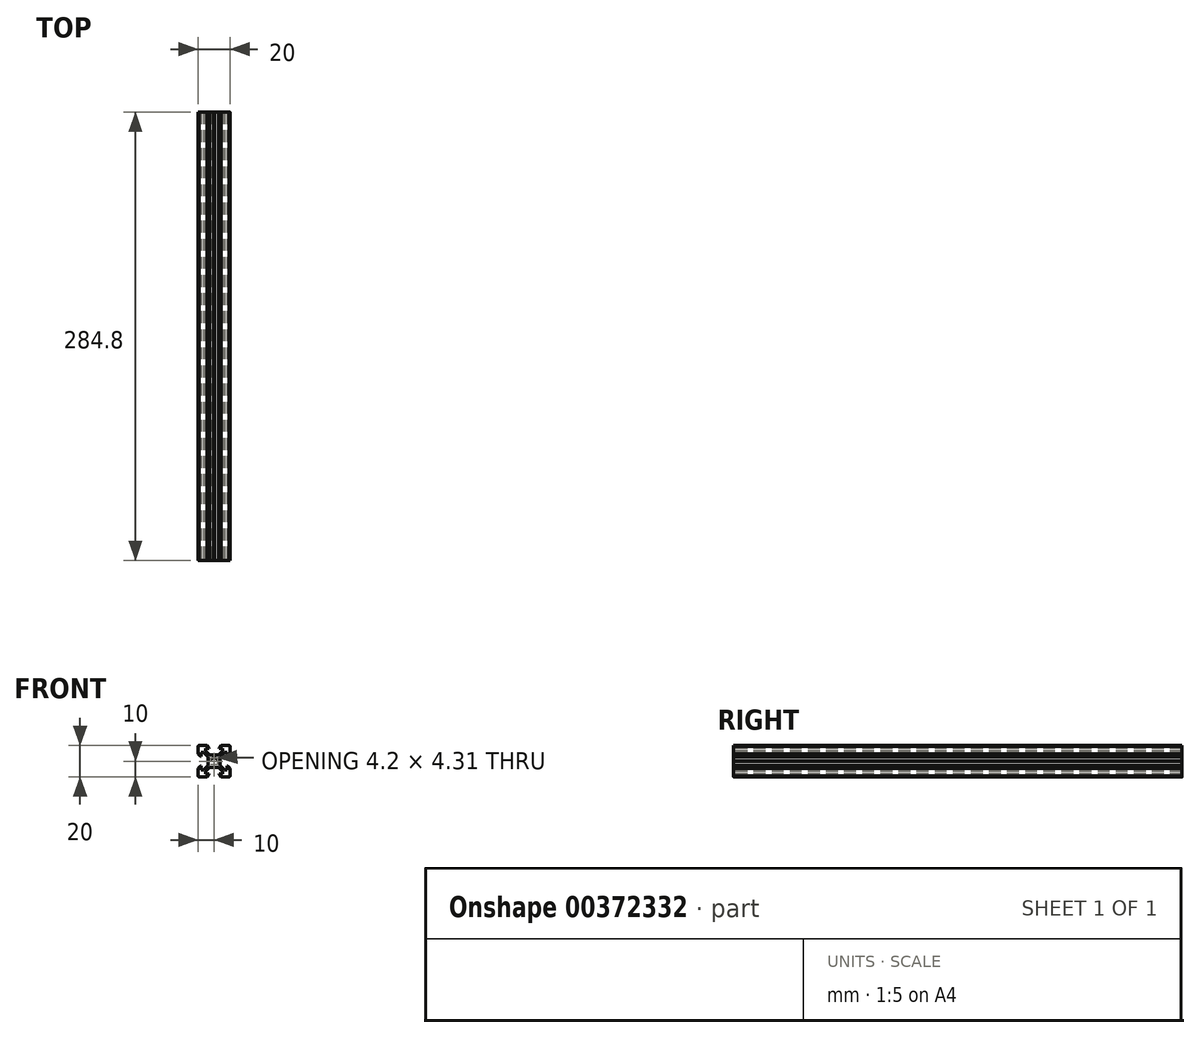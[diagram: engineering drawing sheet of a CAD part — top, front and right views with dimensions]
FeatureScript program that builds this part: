
annotation { "Feature Type Name" : "Feature", "Feature Type Description" : "" }
export const myFeature = defineFeature(function(context is Context, id is Id, definition is map)
    precondition{}
    {
        {
            var Q0;
            Q0=qCreatedBy(makeId("Front.planeOp"),FACE);
            var sketch = newSketch(context, id + "F0", { "sketchPlane" : qUnion([Q0])});
            skFitSpline(sketch, "E0.0", {"points": [v(-8.2, 3.13) * mm, v(-8.2, 3.92) * mm, v(-8.2, 4.7) * mm, v(-8.2, 5.5) * mm]});
            skFitSpline(sketch, "E0.1", {"points": [v(-8.2, 5.5) * mm, v(-7.65, 5.5) * mm, v(-7.1, 5.5) * mm, v(-6.56, 5.5) * mm]});
            skFitSpline(sketch, "E0.2", {"points": [v(-6.56, 5.5) * mm, v(-5.67, 4.61) * mm, v(-4.79, 3.73) * mm, v(-3.9, 2.84) * mm]});
            skFitSpline(sketch, "E0.3", {"points": [v(-2.84, 3.9) * mm, v(-3.73, 4.79) * mm, v(-4.61, 5.67) * mm, v(-5.5, 6.56) * mm]});
            skFitSpline(sketch, "E0.4", {"points": [v(-5.5, 6.56) * mm, v(-5.5, 7.1) * mm, v(-5.5, 7.65) * mm, v(-5.5, 8.2) * mm]});
            skFitSpline(sketch, "E0.5", {"points": [v(-5.5, 8.2) * mm, v(-4.7, 8.2) * mm, v(-3.92, 8.2) * mm, v(-3.12, 8.2) * mm]});
            skFitSpline(sketch, "E0.6", {"points": [v(-3.12, 8.2) * mm, v(-3.12, 8.32) * mm, v(-3.12, 8.43) * mm, v(-3.12, 8.55) * mm]});
            skFitSpline(sketch, "E0.7", {"points": [v(-10, 4.58) * mm, v(-9.51, 4.1) * mm, v(-9.03, 3.61) * mm, v(-8.54, 3.13) * mm]});
            skFitSpline(sketch, "E0.8", {"points": [v(-8.54, 3.13) * mm, v(-8.43, 3.13) * mm, v(-8.31, 3.13) * mm, v(-8.2, 3.13) * mm]});
            skFitSpline(sketch, "E0.9", {"points": [v(-10, 9.5) * mm, v(-10, 7.86) * mm, v(-10, 6.22) * mm, v(-10, 4.58) * mm]});
            skFitSpline(sketch, "E0.10", {"points": [v(-9.5, 10) * mm, v(-9.57, 10) * mm, v(-9.63, 9.99) * mm, v(-9.7, 9.96) * mm, v(-9.75, 9.94) * mm, v(-9.8, 9.9) * mm, v(-9.85, 9.85) * mm, v(-9.9, 9.8) * mm, v(-9.94, 9.75) * mm, v(-9.96, 9.7) * mm, v(-9.99, 9.63) * mm, v(-10, 9.57) * mm, v(-10, 9.5) * mm]});
            skFitSpline(sketch, "E0.11", {"points": [v(-4.58, 10) * mm, v(-6.22, 10) * mm, v(-7.86, 10) * mm, v(-9.5, 10) * mm]});
            skFitSpline(sketch, "E0.12", {"points": [v(-3.9, 2.84) * mm, v(-3.9, 1.96) * mm, v(-3.9, 1.09) * mm, v(-3.9, 0.21) * mm]});
            skFitSpline(sketch, "E0.13", {"points": [v(-3.9, 0.21) * mm, v(-3.83, 0.14) * mm, v(-3.76, 0.07) * mm, v(-3.69, 0) * mm]});
            skFitSpline(sketch, "E0.14", {"points": [v(-0.2, 3.9) * mm, v(-1.09, 3.9) * mm, v(-1.96, 3.9) * mm, v(-2.84, 3.9) * mm]});
            skFitSpline(sketch, "E0.15", {"points": [v(0, 3.7) * mm, v(-0.07, 3.76) * mm, v(-0.14, 3.83) * mm, v(-0.2, 3.9) * mm]});
            skFitSpline(sketch, "E0.16", {"points": [v(2.1, 0) * mm, v(2.1, 0.27) * mm, v(2, 0.82) * mm, v(1.52, 1.52) * mm, v(0.82, 2) * mm, v(0, 2.15) * mm, v(-0.82, 2) * mm, v(-1.52, 1.52) * mm, v(-2, 0.82) * mm, v(-2.1, 0.27) * mm, v(-2.1, 0) * mm]});
            skFitSpline(sketch, "E1.0", {"points": [v(-8.2, 3.13) * mm, v(-8.2, 3.92) * mm, v(-8.2, 4.7) * mm, v(-8.2, 5.5) * mm]});
            skFitSpline(sketch, "E1.1", {"points": [v(-8.2, 5.5) * mm, v(-7.65, 5.5) * mm, v(-7.1, 5.5) * mm, v(-6.56, 5.5) * mm]});
            skFitSpline(sketch, "E1.2", {"points": [v(-6.56, 5.5) * mm, v(-5.67, 4.61) * mm, v(-4.79, 3.73) * mm, v(-3.9, 2.84) * mm]});
            skFitSpline(sketch, "E1.3", {"points": [v(-2.84, 3.9) * mm, v(-3.73, 4.79) * mm, v(-4.61, 5.67) * mm, v(-5.5, 6.56) * mm]});
            skFitSpline(sketch, "E1.4", {"points": [v(-5.5, 6.56) * mm, v(-5.5, 7.1) * mm, v(-5.5, 7.65) * mm, v(-5.5, 8.2) * mm]});
            skFitSpline(sketch, "E1.5", {"points": [v(-5.5, 8.2) * mm, v(-4.7, 8.2) * mm, v(-3.92, 8.2) * mm, v(-3.12, 8.2) * mm]});
            skFitSpline(sketch, "E1.6", {"points": [v(-3.12, 8.2) * mm, v(-3.12, 8.32) * mm, v(-3.12, 8.43) * mm, v(-3.12, 8.55) * mm]});
            skFitSpline(sketch, "E1.7", {"points": [v(-10, 4.58) * mm, v(-9.51, 4.1) * mm, v(-9.03, 3.61) * mm, v(-8.54, 3.13) * mm]});
            skFitSpline(sketch, "E1.8", {"points": [v(-8.54, 3.13) * mm, v(-8.43, 3.13) * mm, v(-8.31, 3.13) * mm, v(-8.2, 3.13) * mm]});
            skFitSpline(sketch, "E1.9", {"points": [v(-10, 9.5) * mm, v(-10, 7.86) * mm, v(-10, 6.22) * mm, v(-10, 4.58) * mm]});
            skFitSpline(sketch, "E1.10", {"points": [v(-9.5, 10) * mm, v(-9.57, 10) * mm, v(-9.63, 9.99) * mm, v(-9.7, 9.96) * mm, v(-9.75, 9.94) * mm, v(-9.8, 9.9) * mm, v(-9.85, 9.85) * mm, v(-9.9, 9.8) * mm, v(-9.94, 9.75) * mm, v(-9.96, 9.7) * mm, v(-9.99, 9.63) * mm, v(-10, 9.57) * mm, v(-10, 9.5) * mm]});
            skFitSpline(sketch, "E1.11", {"points": [v(-4.58, 10) * mm, v(-6.22, 10) * mm, v(-7.86, 10) * mm, v(-9.5, 10) * mm]});
            skFitSpline(sketch, "E1.12", {"points": [v(-3.9, 2.84) * mm, v(-3.9, 1.96) * mm, v(-3.9, 1.09) * mm, v(-3.9, 0.21) * mm]});
            skFitSpline(sketch, "E1.13", {"points": [v(-3.9, 0.21) * mm, v(-3.83, 0.14) * mm, v(-3.76, 0.07) * mm, v(-3.69, 0) * mm]});
            skFitSpline(sketch, "E1.14", {"points": [v(-0.2, 3.9) * mm, v(-1.09, 3.9) * mm, v(-1.96, 3.9) * mm, v(-2.84, 3.9) * mm]});
            skFitSpline(sketch, "E1.15", {"points": [v(0, 3.7) * mm, v(-0.07, 3.76) * mm, v(-0.14, 3.83) * mm, v(-0.2, 3.9) * mm]});
            skFitSpline(sketch, "E1.16", {"points": [v(2.1, 0) * mm, v(2.1, 0.27) * mm, v(2, 0.82) * mm, v(1.52, 1.52) * mm, v(0.82, 2) * mm, v(0, 2.15) * mm, v(-0.82, 2) * mm, v(-1.52, 1.52) * mm, v(-2, 0.82) * mm, v(-2.1, 0.27) * mm, v(-2.1, 0) * mm]});
            skFitSpline(sketch, "E2.0", {"points": [v(2.84, 3.9) * mm, v(1.96, 3.9) * mm, v(1.09, 3.9) * mm, v(0.21, 3.9) * mm]});
            skFitSpline(sketch, "E2.1", {"points": [v(0.21, 3.9) * mm, v(0.14, 3.83) * mm, v(0.07, 3.76) * mm, v(0, 3.7) * mm]});
            skFitSpline(sketch, "E2.2", {"points": [v(3.9, 0.2) * mm, v(3.9, 1.09) * mm, v(3.9, 1.96) * mm, v(3.9, 2.84) * mm]});
            skFitSpline(sketch, "E2.3", {"points": [v(3.69, 0) * mm, v(3.76, 0.07) * mm, v(3.83, 0.14) * mm, v(3.9, 0.2) * mm]});
            skFitSpline(sketch, "E2.4", {"points": [v(3.9, 2.84) * mm, v(4.79, 3.73) * mm, v(5.67, 4.61) * mm, v(6.56, 5.5) * mm]});
            skFitSpline(sketch, "E2.5", {"points": [v(5.5, 6.56) * mm, v(4.61, 5.67) * mm, v(3.73, 4.79) * mm, v(2.84, 3.9) * mm]});
            skFitSpline(sketch, "E2.6", {"points": [v(6.56, 5.5) * mm, v(7.1, 5.5) * mm, v(7.65, 5.5) * mm, v(8.2, 5.5) * mm]});
            skFitSpline(sketch, "E2.7", {"points": [v(8.2, 5.5) * mm, v(8.2, 4.7) * mm, v(8.2, 3.92) * mm, v(8.2, 3.13) * mm]});
            skFitSpline(sketch, "E2.8", {"points": [v(8.2, 3.13) * mm, v(8.31, 3.13) * mm, v(8.43, 3.13) * mm, v(8.54, 3.13) * mm]});
            skFitSpline(sketch, "E2.9", {"points": [v(8.54, 3.13) * mm, v(9.03, 3.61) * mm, v(9.51, 4.1) * mm, v(10, 4.58) * mm]});
            skFitSpline(sketch, "E2.10", {"points": [v(10, 4.58) * mm, v(10, 6.22) * mm, v(10, 7.86) * mm, v(10, 9.5) * mm]});
            skFitSpline(sketch, "E2.11", {"points": [v(5.5, 8.2) * mm, v(5.5, 7.65) * mm, v(5.5, 7.1) * mm, v(5.5, 6.56) * mm]});
            skFitSpline(sketch, "E2.12", {"points": [v(3.13, 8.2) * mm, v(3.92, 8.2) * mm, v(4.7, 8.2) * mm, v(5.5, 8.2) * mm]});
            skFitSpline(sketch, "E2.13", {"points": [v(3.13, 8.55) * mm, v(3.13, 8.43) * mm, v(3.13, 8.32) * mm, v(3.13, 8.2) * mm]});
            skFitSpline(sketch, "E2.14", {"points": [v(9.5, 10) * mm, v(7.86, 10) * mm, v(6.22, 10) * mm, v(4.58, 10) * mm]});
            skFitSpline(sketch, "E2.15", {"points": [v(10, 9.5) * mm, v(10, 9.57) * mm, v(9.99, 9.63) * mm, v(9.96, 9.7) * mm, v(9.94, 9.75) * mm, v(9.9, 9.8) * mm, v(9.85, 9.85) * mm, v(9.8, 9.9) * mm, v(9.75, 9.94) * mm, v(9.7, 9.96) * mm, v(9.63, 9.99) * mm, v(9.57, 10) * mm, v(9.5, 10) * mm]});
            skFitSpline(sketch, "E2.16", {"points": [v(4.58, 10) * mm, v(4.1, 9.52) * mm, v(3.61, 9.03) * mm, v(3.13, 8.55) * mm]});
            skLineSegment(sketch, "E3", {"start": v(-4.58, 10) * mm, "end": v(-3.12, 8.55) * mm});
            skFitSpline(sketch, "E4.MirrorCS", {"points": [v(-3.9, -0.2) * mm, v(-3.83, -0.14) * mm, v(-3.76, -0.07) * mm, v(-3.69, 0) * mm]});
            skFitSpline(sketch, "E5.MirrorCS", {"points": [v(0, -3.7) * mm, v(-0.07, -3.76) * mm, v(-0.14, -3.83) * mm, v(-0.21, -3.9) * mm]});
            skFitSpline(sketch, "E6.MirrorCS", {"points": [v(-8.55, -3.12) * mm, v(-8.43, -3.12) * mm, v(-8.32, -3.12) * mm, v(-8.2, -3.12) * mm]});
            skFitSpline(sketch, "E7.MirrorCS", {"points": [v(0.2, -3.9) * mm, v(0.14, -3.83) * mm, v(0.07, -3.76) * mm, v(0, -3.7) * mm]});
            skFitSpline(sketch, "E8.MirrorCS", {"points": [v(-3.13, -8.2) * mm, v(-3.13, -8.31) * mm, v(-3.13, -8.43) * mm, v(-3.13, -8.54) * mm]});
            skFitSpline(sketch, "E9.MirrorCS", {"points": [v(-3.9, -0.2) * mm, v(-3.83, -0.14) * mm, v(-3.76, -0.07) * mm, v(-3.69, 0) * mm]});
            skFitSpline(sketch, "E10.MirrorCS", {"points": [v(-8.55, -3.12) * mm, v(-8.43, -3.12) * mm, v(-8.32, -3.12) * mm, v(-8.2, -3.12) * mm]});
            skFitSpline(sketch, "E11.MirrorCS", {"points": [v(0, -3.7) * mm, v(-0.07, -3.76) * mm, v(-0.14, -3.83) * mm, v(-0.21, -3.9) * mm]});
            skFitSpline(sketch, "E12.MirrorCS", {"points": [v(-3.13, -8.2) * mm, v(-3.13, -8.31) * mm, v(-3.13, -8.43) * mm, v(-3.13, -8.54) * mm]});
            skFitSpline(sketch, "E13.MirrorCS", {"points": [v(3.12, -8.55) * mm, v(3.12, -8.43) * mm, v(3.12, -8.32) * mm, v(3.12, -8.2) * mm]});
            skFitSpline(sketch, "E14.MirrorCS", {"points": [v(3.69, 0) * mm, v(3.76, -0.07) * mm, v(3.83, -0.14) * mm, v(3.9, -0.21) * mm]});
            skFitSpline(sketch, "E15.MirrorCS", {"points": [v(8.2, -3.13) * mm, v(8.31, -3.13) * mm, v(8.43, -3.13) * mm, v(8.54, -3.13) * mm]});
            skFitSpline(sketch, "E16.MirrorCS", {"points": [v(-8.2, -5.5) * mm, v(-7.65, -5.5) * mm, v(-7.1, -5.5) * mm, v(-6.56, -5.5) * mm]});
            skFitSpline(sketch, "E17.MirrorCS", {"points": [v(-2.84, -3.9) * mm, v(-3.73, -4.79) * mm, v(-4.61, -5.67) * mm, v(-5.5, -6.56) * mm]});
            skFitSpline(sketch, "E18.MirrorCS", {"points": [v(-5.5, -8.2) * mm, v(-4.7, -8.2) * mm, v(-3.92, -8.2) * mm, v(-3.13, -8.2) * mm]});
            skFitSpline(sketch, "E19.MirrorCS", {"points": [v(-5.5, -6.56) * mm, v(-5.5, -7.1) * mm, v(-5.5, -7.65) * mm, v(-5.5, -8.2) * mm]});
            skFitSpline(sketch, "E20.MirrorCS", {"points": [v(-0.21, -3.9) * mm, v(-1.09, -3.9) * mm, v(-1.96, -3.9) * mm, v(-2.84, -3.9) * mm]});
            skFitSpline(sketch, "E21.MirrorCS", {"points": [v(-8.2, -3.12) * mm, v(-8.2, -3.92) * mm, v(-8.2, -4.7) * mm, v(-8.2, -5.5) * mm]});
            skFitSpline(sketch, "E22.MirrorCS", {"points": [v(-10, -4.58) * mm, v(-9.52, -4.1) * mm, v(-9.03, -3.6) * mm, v(-8.55, -3.12) * mm]});
            skFitSpline(sketch, "E23.MirrorCS", {"points": [v(-10, -9.5) * mm, v(-10, -7.86) * mm, v(-10, -6.22) * mm, v(-10, -4.58) * mm]});
            skFitSpline(sketch, "E24.MirrorCS", {"points": [v(-9.5, -10) * mm, v(-9.57, -10) * mm, v(-9.63, -9.99) * mm, v(-9.7, -9.96) * mm, v(-9.75, -9.94) * mm, v(-9.8, -9.9) * mm, v(-9.85, -9.85) * mm, v(-9.9, -9.8) * mm, v(-9.94, -9.75) * mm, v(-9.96, -9.7) * mm, v(-9.99, -9.63) * mm, v(-10, -9.57) * mm, v(-10, -9.5) * mm]});
            skFitSpline(sketch, "E25.MirrorCS", {"points": [v(-4.58, -10) * mm, v(-6.22, -10) * mm, v(-7.86, -10) * mm, v(-9.5, -10) * mm]});
            skFitSpline(sketch, "E26.MirrorCS", {"points": [v(-3.9, -2.84) * mm, v(-3.9, -1.96) * mm, v(-3.9, -1.09) * mm, v(-3.9, -0.21) * mm]});
            skFitSpline(sketch, "E27.MirrorCS", {"points": [v(-6.56, -5.5) * mm, v(-5.67, -4.61) * mm, v(-4.79, -3.73) * mm, v(-3.9, -2.84) * mm]});
            skFitSpline(sketch, "E28.MirrorCS", {"points": [v(2.1, 0) * mm, v(2.1, -0.27) * mm, v(2, -0.82) * mm, v(1.52, -1.52) * mm, v(0.82, -2) * mm, v(0, -2.15) * mm, v(-0.82, -2) * mm, v(-1.52, -1.52) * mm, v(-2, -0.82) * mm, v(-2.1, -0.27) * mm, v(-2.1, 0) * mm]});
            skFitSpline(sketch, "E29.MirrorCS", {"points": [v(4.58, -10) * mm, v(4.1, -9.52) * mm, v(3.6, -9.03) * mm, v(3.12, -8.55) * mm]});
            skFitSpline(sketch, "E30.MirrorCS", {"points": [v(-6.56, -5.5) * mm, v(-5.67, -4.61) * mm, v(-4.79, -3.73) * mm, v(-3.9, -2.84) * mm]});
            skFitSpline(sketch, "E31.MirrorCS", {"points": [v(10, -4.58) * mm, v(10, -6.22) * mm, v(10, -7.86) * mm, v(10, -9.5) * mm]});
            skLineSegment(sketch, "E32.MirrorCS", {"start": v(-4.58, -10) * mm, "end": v(-3.13, -8.54) * mm});
            skFitSpline(sketch, "E33.MirrorCS", {"points": [v(-4.58, -10) * mm, v(-6.22, -10) * mm, v(-7.86, -10) * mm, v(-9.5, -10) * mm]});
            skFitSpline(sketch, "E34.MirrorCS", {"points": [v(6.56, -5.5) * mm, v(7.1, -5.5) * mm, v(7.65, -5.5) * mm, v(8.2, -5.5) * mm]});
            skFitSpline(sketch, "E35.MirrorCS", {"points": [v(-10, -4.58) * mm, v(-9.52, -4.1) * mm, v(-9.03, -3.6) * mm, v(-8.55, -3.12) * mm]});
            skFitSpline(sketch, "E36.MirrorCS", {"points": [v(-5.5, -6.56) * mm, v(-5.5, -7.1) * mm, v(-5.5, -7.65) * mm, v(-5.5, -8.2) * mm]});
            skFitSpline(sketch, "E37.MirrorCS", {"points": [v(3.12, -8.2) * mm, v(3.92, -8.2) * mm, v(4.7, -8.2) * mm, v(5.5, -8.2) * mm]});
            skFitSpline(sketch, "E38.MirrorCS", {"points": [v(-8.2, -5.5) * mm, v(-7.65, -5.5) * mm, v(-7.1, -5.5) * mm, v(-6.56, -5.5) * mm]});
            skFitSpline(sketch, "E39.MirrorCS", {"points": [v(-8.2, -3.12) * mm, v(-8.2, -3.92) * mm, v(-8.2, -4.7) * mm, v(-8.2, -5.5) * mm]});
            skFitSpline(sketch, "E40.MirrorCS", {"points": [v(10, -9.5) * mm, v(10, -9.57) * mm, v(9.99, -9.63) * mm, v(9.96, -9.7) * mm, v(9.94, -9.75) * mm, v(9.9, -9.8) * mm, v(9.85, -9.85) * mm, v(9.8, -9.9) * mm, v(9.75, -9.94) * mm, v(9.7, -9.96) * mm, v(9.63, -9.99) * mm, v(9.57, -10) * mm, v(9.5, -10) * mm]});
            skFitSpline(sketch, "E41.MirrorCS", {"points": [v(2.1, 0) * mm, v(2.1, -0.27) * mm, v(2, -0.82) * mm, v(1.52, -1.52) * mm, v(0.82, -2) * mm, v(0, -2.15) * mm, v(-0.82, -2) * mm, v(-1.52, -1.52) * mm, v(-2, -0.82) * mm, v(-2.1, -0.27) * mm, v(-2.1, 0) * mm]});
            skFitSpline(sketch, "E42.MirrorCS", {"points": [v(2.84, -3.9) * mm, v(1.96, -3.9) * mm, v(1.09, -3.9) * mm, v(0.2, -3.9) * mm]});
            skFitSpline(sketch, "E43.MirrorCS", {"points": [v(-10, -9.5) * mm, v(-10, -7.86) * mm, v(-10, -6.22) * mm, v(-10, -4.58) * mm]});
            skFitSpline(sketch, "E44.MirrorCS", {"points": [v(8.2, -5.5) * mm, v(8.2, -4.7) * mm, v(8.2, -3.92) * mm, v(8.2, -3.13) * mm]});
            skFitSpline(sketch, "E45.MirrorCS", {"points": [v(8.54, -3.13) * mm, v(9.03, -3.61) * mm, v(9.51, -4.1) * mm, v(10, -4.58) * mm]});
            skFitSpline(sketch, "E46.MirrorCS", {"points": [v(3.9, -2.84) * mm, v(4.79, -3.73) * mm, v(5.67, -4.61) * mm, v(6.56, -5.5) * mm]});
            skFitSpline(sketch, "E47.MirrorCS", {"points": [v(-9.5, -10) * mm, v(-9.57, -10) * mm, v(-9.63, -9.99) * mm, v(-9.7, -9.96) * mm, v(-9.75, -9.94) * mm, v(-9.8, -9.9) * mm, v(-9.85, -9.85) * mm, v(-9.9, -9.8) * mm, v(-9.94, -9.75) * mm, v(-9.96, -9.7) * mm, v(-9.99, -9.63) * mm, v(-10, -9.57) * mm, v(-10, -9.5) * mm]});
            skFitSpline(sketch, "E48.MirrorCS", {"points": [v(-0.21, -3.9) * mm, v(-1.09, -3.9) * mm, v(-1.96, -3.9) * mm, v(-2.84, -3.9) * mm]});
            skFitSpline(sketch, "E49.MirrorCS", {"points": [v(5.5, -6.56) * mm, v(4.61, -5.67) * mm, v(3.73, -4.79) * mm, v(2.84, -3.9) * mm]});
            skFitSpline(sketch, "E50.MirrorCS", {"points": [v(-2.84, -3.9) * mm, v(-3.73, -4.79) * mm, v(-4.61, -5.67) * mm, v(-5.5, -6.56) * mm]});
            skFitSpline(sketch, "E51.MirrorCS", {"points": [v(-5.5, -8.2) * mm, v(-4.7, -8.2) * mm, v(-3.92, -8.2) * mm, v(-3.13, -8.2) * mm]});
            skFitSpline(sketch, "E52.MirrorCS", {"points": [v(5.5, -8.2) * mm, v(5.5, -7.65) * mm, v(5.5, -7.1) * mm, v(5.5, -6.56) * mm]});
            skFitSpline(sketch, "E53.MirrorCS", {"points": [v(3.9, -0.21) * mm, v(3.9, -1.09) * mm, v(3.9, -1.96) * mm, v(3.9, -2.84) * mm]});
            skFitSpline(sketch, "E54.MirrorCS", {"points": [v(-3.9, -2.84) * mm, v(-3.9, -1.96) * mm, v(-3.9, -1.09) * mm, v(-3.9, -0.21) * mm]});
            skFitSpline(sketch, "E55.MirrorCS", {"points": [v(9.5, -10) * mm, v(7.86, -10) * mm, v(6.22, -10) * mm, v(4.58, -10) * mm]});
            skLineSegment(sketch, "E56.MirrorCS", {"start": v(0, 3.7) * mm, "end": v(0, 0) * mm, "construction": true});
            skLineSegment(sketch, "E57.MirrorCS", {"start": v(0, -3.7) * mm, "end": v(0, 0) * mm, "construction": true});
            skSolve(sketch);
        }
        {
            var Q0;
            Q0 = qSketchRegion(id + "F0", true);
            extrude(context, id + "F1", {"entities" : qUnion([Q0]), "oppositeDirection" : true, "depth" : 304.8 * mm - 20 * mm});
        }
    });
